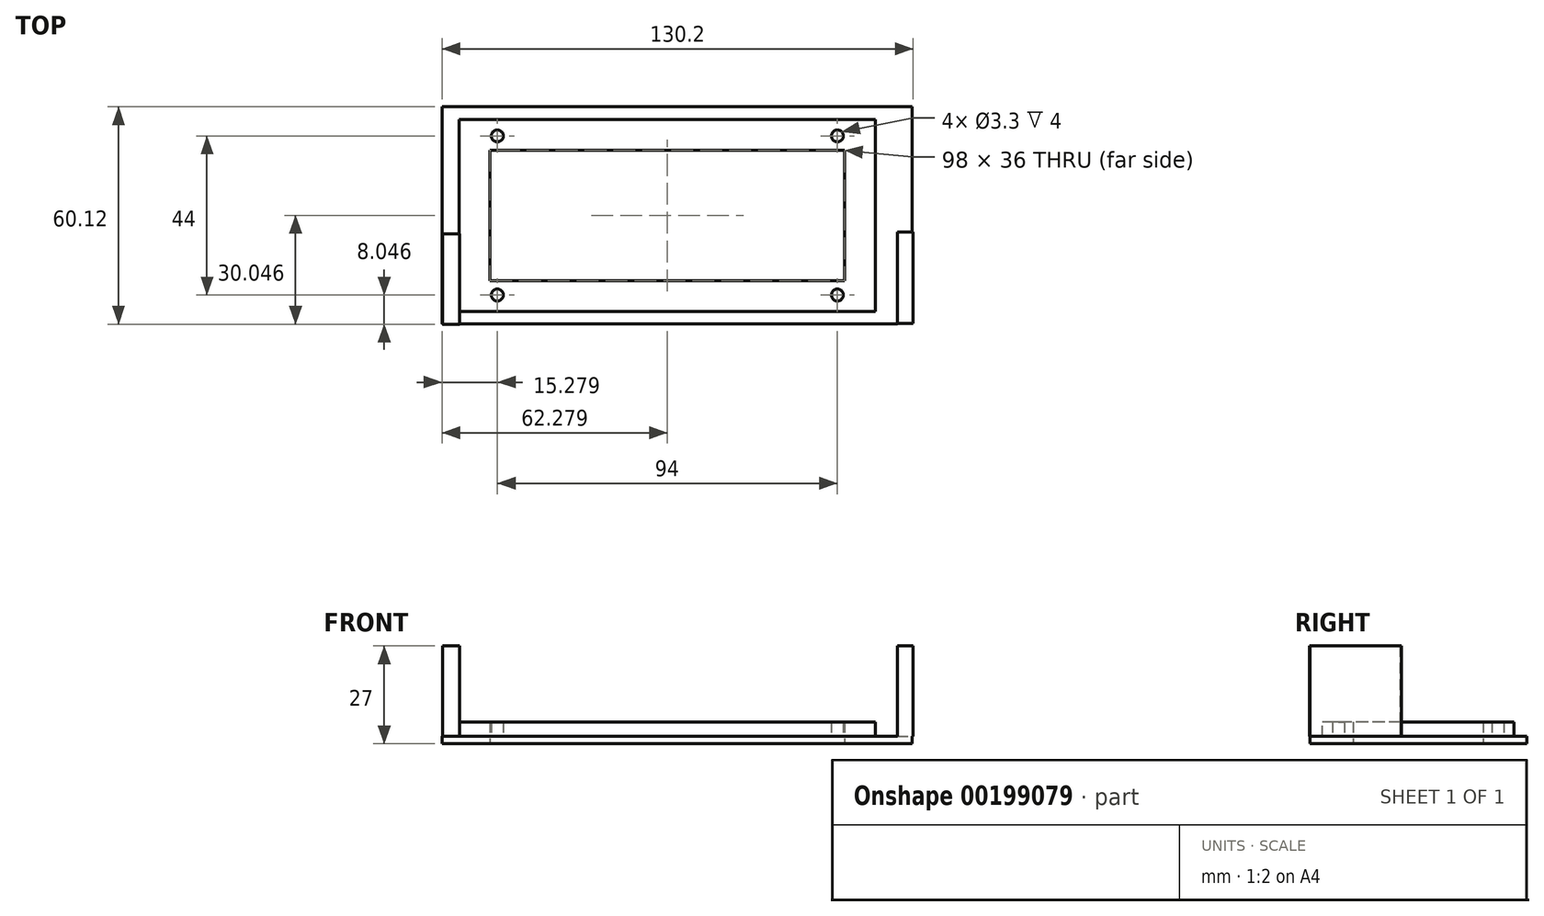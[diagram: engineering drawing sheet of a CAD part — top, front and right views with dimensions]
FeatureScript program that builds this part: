
annotation { "Feature Type Name" : "Feature", "Feature Type Description" : "" }
export const myFeature = defineFeature(function(context is Context, id is Id, definition is map)
    precondition{}
    {
        {
            var Q0;
            Q0=qCreatedBy(makeId("Top.planeOp"),FACE);
            var sketch = newSketch(context, id + "F0", { "sketchPlane" : qUnion([Q0])});
            skLineSegment(sketch, "E0.bottom", {"start": v(-67.47, 31.58) * mm, "end": v(47.53, 31.58) * mm});
            skLineSegment(sketch, "E0.top", {"start": v(-67.47, -21.42) * mm, "end": v(47.53, -21.42) * mm});
            skLineSegment(sketch, "E0.left", {"start": v(-67.47, 31.58) * mm, "end": v(-67.47, -21.42) * mm});
            skLineSegment(sketch, "E0.right", {"start": v(47.53, 31.58) * mm, "end": v(47.53, -21.42) * mm});
            skLineSegment(sketch, "E1", {"start": v(-9.97, 31.58) * mm, "end": v(-9.97, -21.42) * mm, "construction": true});
            skLineSegment(sketch, "E2", {"start": v(-67.47, 5.08) * mm, "end": v(47.53, 5.08) * mm, "construction": true});
            skLineSegment(sketch, "E3.bottom", {"start": v(39.03, 23.08) * mm, "end": v(-58.97, 23.08) * mm});
            skLineSegment(sketch, "E3.top", {"start": v(39.03, -12.92) * mm, "end": v(-58.97, -12.92) * mm});
            skLineSegment(sketch, "E3.left", {"start": v(39.03, 23.08) * mm, "end": v(39.03, -12.92) * mm});
            skLineSegment(sketch, "E3.right", {"start": v(-58.97, 23.08) * mm, "end": v(-58.97, -12.92) * mm});
            skPoint(sketch, "E3.middle", {"position": v(-9.97, 5.08) * mm});
            skPoint(sketch, "E4", {"position": v(-56.97, 27.08) * mm});
            skPoint(sketch, "E5.MirrorP", {"position": v(37.03, 27.08) * mm});
            skPoint(sketch, "E6.MirrorP", {"position": v(-56.97, -16.92) * mm});
            skPoint(sketch, "E7.MirrorP", {"position": v(37.03, -16.92) * mm});
            skSolve(sketch);
        }
        {
            var Q0;
            Q0=makeQuery(id+"F0.imprint","IMPRINT",FACE,{"disambiguationData":[TD([[makeQuery(id+"F0.imprint","IMPRINT",EDGE,{"derivedFrom":sQuery(id+"F0.wireOp",EDGE,"E0.bottom")}),-1.0]])]});
            extrude(context, id + "F1", {"entities" : qUnion([Q0]), "depth" : 4 * mm});
        }
        {
            var Q0;
            Q0=qCreatedBy(makeId("Top.planeOp"),FACE);
            var sketch = newSketch(context, id + "F2", { "sketchPlane" : qUnion([Q0])});
            skLineSegment(sketch, "E8.bottom", {"start": v(-72.25, 35.15) * mm, "end": v(57.75, 35.15) * mm});
            skLineSegment(sketch, "E8.top", {"start": v(-72.25, -24.85) * mm, "end": v(57.75, -24.85) * mm});
            skLineSegment(sketch, "E8.left", {"start": v(-72.25, 35.15) * mm, "end": v(-72.25, -24.85) * mm});
            skLineSegment(sketch, "E8.right", {"start": v(57.75, 35.15) * mm, "end": v(57.75, -24.85) * mm});
            skPoint(sketch, "E8.middle", {"position": v(-7.25, 5.15) * mm});
            skSolve(sketch);
        }
        {
            var Q0;
            Q0=makeQuery(id+"F2.imprint","IMPRINT",FACE,{"disambiguationData":[TD([[makeQuery(id+"F2.imprint","IMPRINT",EDGE,{"derivedFrom":sQuery(id+"F2.wireOp",EDGE,"E8.bottom")}),-1.0]])]});
            extrude(context, id + "F3", {"entities" : qUnion([Q0]), "operationType" : NewBodyOperationType.ADD, "oppositeDirection" : true, "depth" : 2 * mm});
        }
        {
            var Q0;
            Q0=makeQuery(id+"F0.imprint","IMPRINT",FACE,{"disambiguationData":[TD([[makeQuery(id+"F0.imprint","IMPRINT",EDGE,{"derivedFrom":sQuery(id+"F0.wireOp",EDGE,"E3.bottom")}),1.0]])]});
            extrude(context, id + "F4", {"entities" : qUnion([Q0]), "operationType" : NewBodyOperationType.REMOVE, "endBound" : BoundingType.THROUGH_ALL, "oppositeDirection" : true, "depth" : 25 * mm});
        }
        {
            var Q0;
            Q0=sQuery(id+"F0.wireOp",VERTEX,"E4");
            var Q1;
            Q1=sQuery(id+"F0.wireOp",VERTEX,"E6.MirrorP");
            var Q2;
            Q2=sQuery(id+"F0.wireOp",VERTEX,"E7.MirrorP");
            var Q3;
            Q3=sQuery(id+"F0.wireOp",VERTEX,"E5.MirrorP");
            var Q4;
            Q4=makeQuery(id+"F1.opExtrude","SWEPT_BODY",BODY,{"disambiguationData":[OSD([sQuery(id+"F0.wireOp",EDGE,"E0.bottom"),sQuery(id+"F0.wireOp",EDGE,"E0.top"),sQuery(id+"F0.wireOp",EDGE,"E0.left"),sQuery(id+"F0.wireOp",EDGE,"E0.right"),sQuery(id+"F0.wireOp",EDGE,"E3.bottom"),sQuery(id+"F0.wireOp",EDGE,"E3.top"),sQuery(id+"F0.wireOp",EDGE,"E3.left"),sQuery(id+"F0.wireOp",EDGE,"E3.right")])]});
            hole(context, id + "F5", {"style" : HoleStyle.SIMPLE, "endStyle" : HoleEndStyle.THROUGH, "oppositeDirection" : true, "standardTappedOrClearance" : lookupTablePath({ "standard" : "ISO", "fit" : "Normal", "size" : "M3", "type" : "Clearance" }), "standardBlindInLast" : lookupTablePath({ "fit" : "Standard", "standard" : "ISO", "size" : "M3", "type" : "Clearance" }), "holeDiameter" : 3.3 * mm, "startFromSketch" : true, "locations" : qUnion([Q0, Q1, Q2, Q3]), "scope" : qUnion([Q4]), "isTappedThrough" : true});
        }
        {
            var Q0;
            Q0=qCreatedBy(makeId("Top.planeOp"),FACE);
            var sketch = newSketch(context, id + "F6", { "sketchPlane" : qUnion([Q0])});
            skLineSegment(sketch, "E9.bottom", {"start": v(53.6, 0.46) * mm, "end": v(57.95, 0.46) * mm});
            skLineSegment(sketch, "E9.top", {"start": v(53.6, -24.84) * mm, "end": v(57.95, -24.84) * mm});
            skLineSegment(sketch, "E9.left", {"start": v(57.95, 0.46) * mm, "end": v(57.95, -24.84) * mm});
            skLineSegment(sketch, "E9.right", {"start": v(53.6, 0.46) * mm, "end": v(53.6, -24.84) * mm});
            skLineSegment(sketch, "E10.bottom", {"start": v(-67.42, -24.97) * mm, "end": v(-72.16, -24.97) * mm});
            skLineSegment(sketch, "E10.top", {"start": v(-67.42, 0) * mm, "end": v(-72.16, 0) * mm});
            skLineSegment(sketch, "E10.left", {"start": v(-67.42, -24.97) * mm, "end": v(-67.42, 0) * mm});
            skLineSegment(sketch, "E10.right", {"start": v(-72.16, -24.97) * mm, "end": v(-72.16, 0) * mm});
            skSolve(sketch);
        }
        {
            var Q0;
            Q0 = qSketchRegion(id + "F6", true);
            extrude(context, id + "F7", {"entities" : qUnion([Q0]), "operationType" : NewBodyOperationType.ADD, "depth" : 25 * mm});
        }
    });
